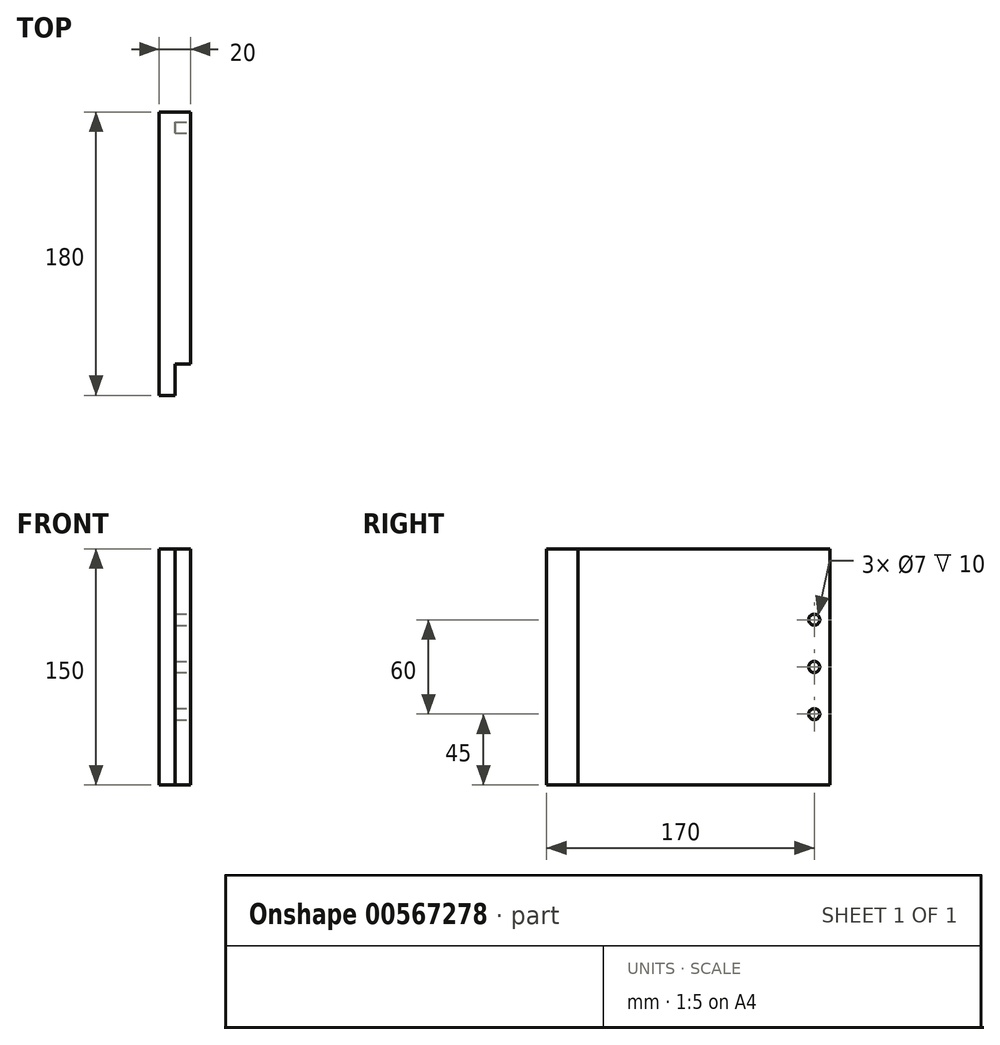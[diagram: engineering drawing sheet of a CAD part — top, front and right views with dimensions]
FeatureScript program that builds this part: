
annotation { "Feature Type Name" : "Feature", "Feature Type Description" : "" }
export const myFeature = defineFeature(function(context is Context, id is Id, definition is map)
    precondition{}
    {
        {
            var Q0;
            Q0=qCreatedBy(makeId("Front.planeOp"),FACE);
            var sketch = newSketch(context, id + "F0", { "sketchPlane" : qUnion([Q0])});
            skLineSegment(sketch, "E0.bottom", {"start": v(0, 0) * mm, "end": v(180, 0) * mm});
            skLineSegment(sketch, "E0.top", {"start": v(0, 150) * mm, "end": v(180, 150) * mm});
            skLineSegment(sketch, "E0.left", {"start": v(0, 0) * mm, "end": v(0, 150) * mm});
            skLineSegment(sketch, "E0.right", {"start": v(180, 0) * mm, "end": v(180, 150) * mm});
            skSolve(sketch);
        }
        {
            var Q0;
            Q0 = qSketchRegion(id + "F0", true);
            extrude(context, id + "F1", {"entities" : qUnion([Q0]), "depth" : 20 * mm, "offsetDistance" : 25 * mm});
        }
        {
            var Q0;
            Q0=makeQuery(id+"F1.opExtrude","CAP_FACE",FACE,{"disambiguationData":[OSD([sQuery(id+"F0.wireOp",EDGE,"E0.bottom"),sQuery(id+"F0.wireOp",EDGE,"E0.top"),sQuery(id+"F0.wireOp",EDGE,"E0.left"),sQuery(id+"F0.wireOp",EDGE,"E0.right")])],"isStart":false});
            var sketch = newSketch(context, id + "F2", { "sketchPlane" : qUnion([Q0])});
            skLineSegment(sketch, "E1", {"start": v(0, 150) * mm, "end": v(20, 150) * mm});
            skLineSegment(sketch, "E2", {"start": v(20, 150) * mm, "end": v(20, 0) * mm});
            skCircle(sketch, "E3", {"center": v(10, 75) * mm, "radius": 3.5 * mm});
            skPoint(sketch, "E3.centerSnap0", {"position": v(10, 150) * mm});
            skPoint(sketch, "E3.centerSnap1", {"position": v(20, 75) * mm});
            skCircle(sketch, "E4", {"center": v(10, 105) * mm, "radius": 3.5 * mm});
            skCircle(sketch, "E5", {"center": v(10, 45) * mm, "radius": 3.5 * mm});
            skSolve(sketch);
        }
        {
            var Q0;
            Q0 = qSketchRegion(id + "F2", true);
            extrude(context, id + "F3", {"entities" : qUnion([Q0]), "operationType" : NewBodyOperationType.REMOVE, "oppositeDirection" : true, "depth" : 10 * mm, "offsetDistance" : 25 * mm});
        }
        {
            var Q0;
            Q0=makeQuery(id+"F1.opExtrude","CAP_FACE",FACE,{"disambiguationData":[OSD([sQuery(id+"F0.wireOp",EDGE,"E0.bottom"),sQuery(id+"F0.wireOp",EDGE,"E0.top"),sQuery(id+"F0.wireOp",EDGE,"E0.left"),sQuery(id+"F0.wireOp",EDGE,"E0.right")])],"isStart":false});
            var sketch = newSketch(context, id + "F4", { "sketchPlane" : qUnion([Q0])});
            skLineSegment(sketch, "E6", {"start": v(180, 150) * mm, "end": v(160, 150) * mm});
            skLineSegment(sketch, "E7", {"start": v(160, 150) * mm, "end": v(160, 0) * mm});
            skSolve(sketch);
        }
        {
            var Q0;
            Q0=makeQuery(id+"F4.imprint","IMPRINT",FACE,{"disambiguationData":[TD([[makeQuery(id+"F4.imprint","IMPRINT",EDGE,{"derivedFrom":sQuery(id+"F4.wireOp",EDGE,"E6")}),-1.0]])]});
            extrude(context, id + "F5", {"entities" : qUnion([Q0]), "operationType" : NewBodyOperationType.REMOVE, "oppositeDirection" : true, "depth" : 10 * mm, "offsetDistance" : 25 * mm});
        }
        {
            var Q0;
            Q0=makeQuery(id+"F1.opExtrude","SWEPT_BODY",BODY,{"disambiguationData":[OSD([sQuery(id+"F0.wireOp",EDGE,"E0.bottom"),sQuery(id+"F0.wireOp",EDGE,"E0.top"),sQuery(id+"F0.wireOp",EDGE,"E0.left"),sQuery(id+"F0.wireOp",EDGE,"E0.right")])]});
            var Q1;
            Q1=makeQuery(id+"F1.opExtrude","CAP_EDGE",EDGE,{"disambiguationData":[OSD([sQuery(id+"F0.wireOp",EDGE,"E0.top")])],"isStart":true});
            transform(context, id + "F6", {"entities" : qUnion([Q0]), "transformType" : TransformType.ROTATION, "transformAxis" : qUnion([Q1]), "angle" : 180 * degree, "makeCopy" : false});
        }
        {
            var Q0;
            Q0=makeQuery(id+"F1.opExtrude","SWEPT_BODY",BODY,{"disambiguationData":[OSD([sQuery(id+"F0.wireOp",EDGE,"E0.bottom"),sQuery(id+"F0.wireOp",EDGE,"E0.top"),sQuery(id+"F0.wireOp",EDGE,"E0.left"),sQuery(id+"F0.wireOp",EDGE,"E0.right")])]});
            var Q1;
            Q1=makeQuery(id+"F1.opExtrude","CAP_EDGE",EDGE,{"disambiguationData":[OSD([sQuery(id+"F0.wireOp",EDGE,"E0.left")])],"isStart":true});
            transform(context, id + "F7", {"entities" : qUnion([Q0]), "transformType" : TransformType.ROTATION, "transformAxis" : qUnion([Q1]), "angle" : 90 * degree, "oppositeDirection" : true, "makeCopy" : false});
        }
        {
            var Q0;
            Q0=makeQuery(id+"F1.opExtrude","SWEPT_BODY",BODY,{"disambiguationData":[OSD([sQuery(id+"F0.wireOp",EDGE,"E0.bottom"),sQuery(id+"F0.wireOp",EDGE,"E0.top"),sQuery(id+"F0.wireOp",EDGE,"E0.left"),sQuery(id+"F0.wireOp",EDGE,"E0.right")])]});
            var Q1;
            Q1=makeQuery(id+"F1.opExtrude","CAP_EDGE",EDGE,{"disambiguationData":[OSD([sQuery(id+"F0.wireOp",EDGE,"E0.left")])],"isStart":false});
            transform(context, id + "F8", {"entities" : qUnion([Q0]), "transformType" : TransformType.ROTATION, "transformAxis" : qUnion([Q1]), "angle" : 180 * degree, "makeCopy" : false});
        }
    });
